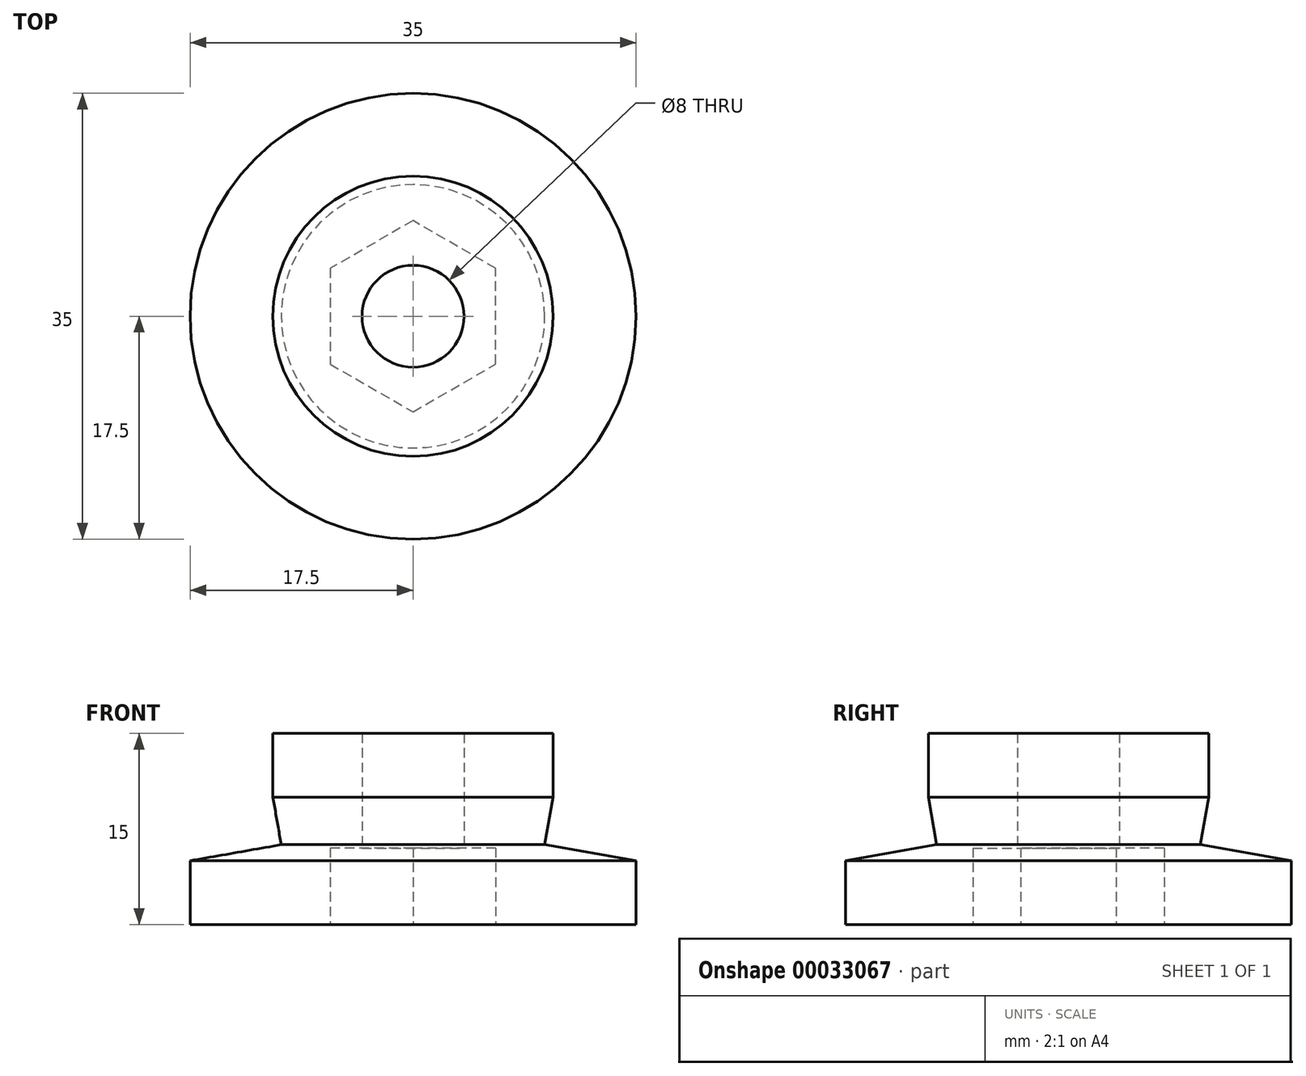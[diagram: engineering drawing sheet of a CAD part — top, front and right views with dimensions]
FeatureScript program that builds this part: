
annotation { "Feature Type Name" : "Feature", "Feature Type Description" : "" }
export const myFeature = defineFeature(function(context is Context, id is Id, definition is map)
    precondition{}
    {
        {
            var Q0;
            Q0=qCreatedBy(makeId("Front.planeOp"),FACE);
            var sketch = newSketch(context, id + "F0", { "sketchPlane" : qUnion([Q0])});
            skLineSegment(sketch, "E0", {"start": v(0, 0) * mm, "end": v(0, 39.05) * mm, "construction": true});
            skLineSegment(sketch, "E1", {"start": v(4, 0) * mm, "end": v(4, 15) * mm});
            skLineSegment(sketch, "E2", {"start": v(4, 15) * mm, "end": v(11, 15) * mm});
            skLineSegment(sketch, "E3", {"start": v(11, 15) * mm, "end": v(11, 10) * mm});
            skLineSegment(sketch, "E4", {"start": v(11, 10) * mm, "end": v(10.34, 6.26) * mm});
            skLineSegment(sketch, "E5", {"start": v(10.34, 6.26) * mm, "end": v(17.5, 5) * mm});
            skLineSegment(sketch, "E6", {"start": v(17.5, 5) * mm, "end": v(17.5, 0) * mm});
            skLineSegment(sketch, "E7", {"start": v(17.5, 0) * mm, "end": v(4, 0) * mm});
            skSolve(sketch);
        }
        {
            var Q0;
            Q0=makeQuery(id+"F0.imprint","IMPRINT",FACE,{"disambiguationData":[TD([[makeQuery(id+"F0.imprint","IMPRINT",EDGE,{"derivedFrom":sQuery(id+"F0.wireOp",EDGE,"E1")}),-1.0]])]});
            var Q1;
            Q1=sQuery(id+"F0.wireOp",EDGE,"E0");
            revolve(context, id + "F1", {"entities" : qUnion([Q0]), "axis" : qUnion([Q1]), "revolveType" : RevolveType.FULL});
        }
        {
            var Q0;
            Q0=makeQuery(id+"F1.opRevolve","SWEPT_FACE",FACE,{"disambiguationData":[OSD([sQuery(id+"F0.wireOp",EDGE,"E7")])]});
            var sketch = newSketch(context, id + "F2", { "sketchPlane" : qUnion([Q0])});
            skCircle(sketch, "E8.cCircle", {"center": v(0, 0) * mm, "radius": 7.5 * mm, "construction": true});
            skLineSegment(sketch, "E8.0", {"start": v(0, -7.5) * mm, "end": v(-6.5, -3.75) * mm});
            skLineSegment(sketch, "E8.1", {"start": v(-6.5, -3.75) * mm, "end": v(-6.5, 3.75) * mm});
            skLineSegment(sketch, "E8.2", {"start": v(-6.5, 3.75) * mm, "end": v(0, 7.5) * mm});
            skLineSegment(sketch, "E8.3", {"start": v(0, 7.5) * mm, "end": v(6.5, 3.75) * mm});
            skLineSegment(sketch, "E8.4", {"start": v(6.5, 3.75) * mm, "end": v(6.5, -3.75) * mm});
            skLineSegment(sketch, "E8.5", {"start": v(6.5, -3.75) * mm, "end": v(0, -7.5) * mm});
            skSolve(sketch);
        }
        {
            var Q0;
            Q0=makeQuery(id+"F2.imprint","IMPRINT",FACE,{"disambiguationData":[TD([[makeQuery(id+"F2.imprint","IMPRINT",EDGE,{"derivedFrom":sQuery(id+"F2.wireOp",EDGE,"E8.0")}),-1.0]])]});
            extrude(context, id + "F3", {"entities" : qUnion([Q0]), "operationType" : NewBodyOperationType.REMOVE, "oppositeDirection" : true, "depth" : 6 * mm});
        }
    });
